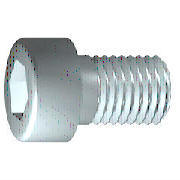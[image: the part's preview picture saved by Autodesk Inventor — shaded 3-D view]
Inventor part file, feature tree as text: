
AUTODESK INVENTOR PART (.ipt)
format: ipt  version: 2022 (Build 260153000, 153)  size: 197,120 bytes
history: native  units: mm (DEFAULTED — no unit token found)
features: sketch x2, other x1, extrude x1, plane x1, fillet x1
ambient origin geometry x7: Origin, YZ Plane, XY Plane, X Axis, Y Axis, Z Axis, Center Point
bodies: Solid1 (feature_tree)
feature tree (6):
  other  "Cuerpo"
  extrude  "Ranura"  Depth=2.5mm
  plane  "Work Plane1"
  fillet  "Fillet2"  Radius=2.5mm
  sketch  "Boceto1"  dims[d1=4.875mm d2=0.276153mm d3=2.5mm]
  sketch  "Boceto2"  dims[d4=1.1mm d5=60.0deg d6=2.5mm d7=2.5mm d8=2.309401mm d9=4.5mm d10=90.0deg d11=10.0mm d12=0.0mm d13=4.875mm d14=0.0mm d15=0.276052mm d16=0.276053mm d17=0.25mm d19=0.0mm d26=6.0mm d27=45.0deg d28=0.0mm d29=0.0mm d30=0.1mm]
